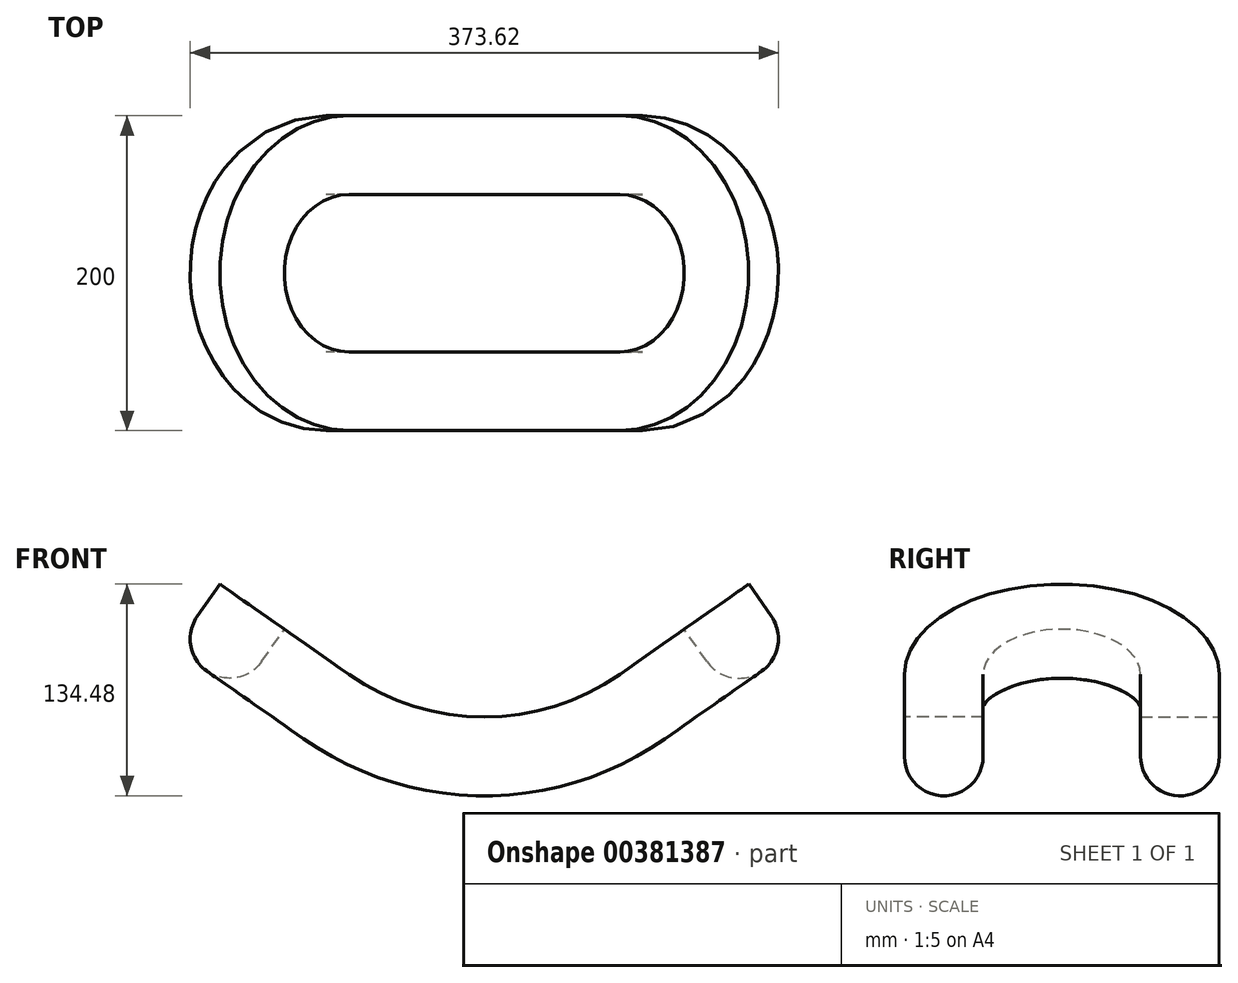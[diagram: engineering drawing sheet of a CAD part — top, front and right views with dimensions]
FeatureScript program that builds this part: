
annotation { "Feature Type Name" : "Feature", "Feature Type Description" : "" }
export const myFeature = defineFeature(function(context is Context, id is Id, definition is map)
    precondition{}
    {
        {
            var Q0;
            Q0=qCreatedBy(makeId("Front.planeOp"),FACE);
            var sketch = newSketch(context, id + "F0", { "sketchPlane" : qUnion([Q0])});
            skArc(sketch, "E0", {"start": v(0, 0) * mm, "mid": v(-45.1, 6.94) * mm, "end": v(-86.04, 27.13) * mm});
            skLineSegment(sketch, "E1", {"start": v(-86.04, 27.13) * mm, "end": v(-167.95, 84.48) * mm});
            skLineSegment(sketch, "E2", {"start": v(-86.04, 27.13) * mm, "end": v(0, 150) * mm, "construction": true});
            skSolve(sketch);
        }
        {
            var Q0;
            Q0=sQuery(id+"F0.wireOp",EDGE,"E1");
            var Q1;
            Q1=sQuery(id+"F0.wireOp",EDGE,"E0");
            extrude(context, id + "F1", {"bodyType" : ToolBodyType.SURFACE, "surfaceEntities" : qUnion([Q0, Q1]), "oppositeDirection" : true, "depth" : 100 * mm});
        }
        {
            var Q0;
            Q0=makeQuery(id+"F1.opExtrude","SWEPT_FACE",FACE,{"disambiguationData":[OSD([sQuery(id+"F0.wireOp",EDGE,"E1")])]});
            var sketch = newSketch(context, id + "F2", { "sketchPlane" : qUnion([Q0])});
            skArc(sketch, "E3", {"start": v(-186.04, 0) * mm, "mid": v(-156.75, -70.71) * mm, "end": v(-86.04, -100) * mm});
            skSolve(sketch);
        }
        {
            var Q0;
            Q0=qCreatedBy(makeId("Right.planeOp"),FACE);
            var sketch = newSketch(context, id + "F3", { "sketchPlane" : qUnion([Q0])});
            skLineSegment(sketch, "E4.bottom", {"start": v(50, 0) * mm, "end": v(100, 0) * mm});
            skLineSegment(sketch, "E4.top", {"start": v(50, -25) * mm, "end": v(100, -25) * mm, "construction": true});
            skLineSegment(sketch, "E4.left", {"start": v(50, 0) * mm, "end": v(50, -25) * mm});
            skLineSegment(sketch, "E4.right", {"start": v(100, 0) * mm, "end": v(100, -25) * mm});
            skArc(sketch, "E5", {"start": v(100, -25) * mm, "mid": v(75, -50) * mm, "end": v(50, -25) * mm});
            skSolve(sketch);
        }
        {
            var Q0;
            Q0=makeQuery(id+"F3.imprint","IMPRINT",FACE,{"disambiguationData":[TD([[makeQuery(id+"F3.imprint","IMPRINT",EDGE,{"derivedFrom":sQuery(id+"F3.wireOp",EDGE,"E4.bottom")}),-1.0]])]});
            var Q1;
            Q1=sQuery(id+"F2.wireOp",EDGE,"E3");
            var Q2;
            Q2=makeQuery(id+"F1.opExtrude","CAP_EDGE",EDGE,{"disambiguationData":[OSD([sQuery(id+"F0.wireOp",EDGE,"E0")])],"isStart":false});
            sweep(context, id + "F4", {"profiles" : qUnion([Q0]), "path" : qUnion([Q1, Q2])});
        }
        {
            var Q0;
            Q0=makeQuery(id+"F4.opSweep","SWEPT_BODY",BODY,{"disambiguationData":[OSD([sQuery(id+"F0.wireOp",EDGE,"E0"),sQuery(id+"F3.wireOp",EDGE,"E4.bottom"),sQuery(id+"F3.wireOp",EDGE,"E4.left"),sQuery(id+"F3.wireOp",EDGE,"E4.right"),sQuery(id+"F3.wireOp",EDGE,"E5")])]});
            var Q1;
            Q1=qCreatedBy(makeId("Front.planeOp"),FACE);
            mirror(context, id + "F5", {"operationType" : NewBodyOperationType.ADD, "entities" : qUnion([Q0]), "mirrorPlane" : qUnion([Q1])});
        }
        {
            var Q0;
            Q0=makeQuery(id+"F4.opSweep","SWEPT_BODY",BODY,{"disambiguationData":[OSD([sQuery(id+"F0.wireOp",EDGE,"E0"),sQuery(id+"F3.wireOp",EDGE,"E4.bottom"),sQuery(id+"F3.wireOp",EDGE,"E4.left"),sQuery(id+"F3.wireOp",EDGE,"E4.right"),sQuery(id+"F3.wireOp",EDGE,"E5")])]});
            var Q1;
            Q1=qCreatedBy(makeId("Right.planeOp"),FACE);
            mirror(context, id + "F6", {"operationType" : NewBodyOperationType.ADD, "entities" : qUnion([Q0]), "mirrorPlane" : qUnion([Q1])});
        }
    });
